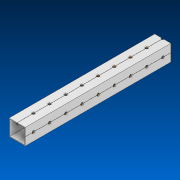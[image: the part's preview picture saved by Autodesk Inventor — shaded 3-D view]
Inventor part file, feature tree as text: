
AUTODESK INVENTOR PART (.ipt)
format: ipt  version: 2022.2 (Build 262287000, 287)  size: 742,400 bytes
history: native  units: in
note: dims shown in document units (in); Inventor stores cm internally (conversion verified against a paired STEP export)
features: other x18, pattern_linear x2, extrude x1, sketch x1
ambient origin geometry x8: Origin, YZ Plane, XZ Plane, XY Plane, X Axis, Y Axis, Z Axis, Center Point
bodies: Solid1 (feature_tree)
feature tree (22):
  extrude  "Extrusion1"  TaperAngle=0.0deg  [1 undecoded]
  other  "Work Axis1"
  other  "Work Axis2"
  pattern_linear  "Rectangular Pattern1"  Count1=9  [1 undecoded]
  pattern_linear  "Rectangular Pattern2"  Spacing1=1.0in  [1 undecoded]
  sketch  "Sketch1"  dims[d0=50.0in d1=0.0in d2=3.5433in d4=1.0in d5=3.1496in d7=1.0in]
  other  "Work Axis3"
  other  "Work Axis4"
  other  "Work Axis5"
  other  "Work Axis6"
  other  "Work Axis7"
  other  "Work Axis8"
  other  "Work Axis9"
  other  "Work Axis10"
  other  "Work Axis11"
  other  "Work Axis12"
  other  "Work Axis63"
  other  "Work Axis64"
  other  "Work Axis65"
  other  "Work Axis66"
  other  "Work Axis67"
  other  "LPattern2"
note: 3 required parameter values undecoded (feature->parameter linkage not recoverable at this tier; creation-order binding heuristic only, values carry confidence <= 0.55)
